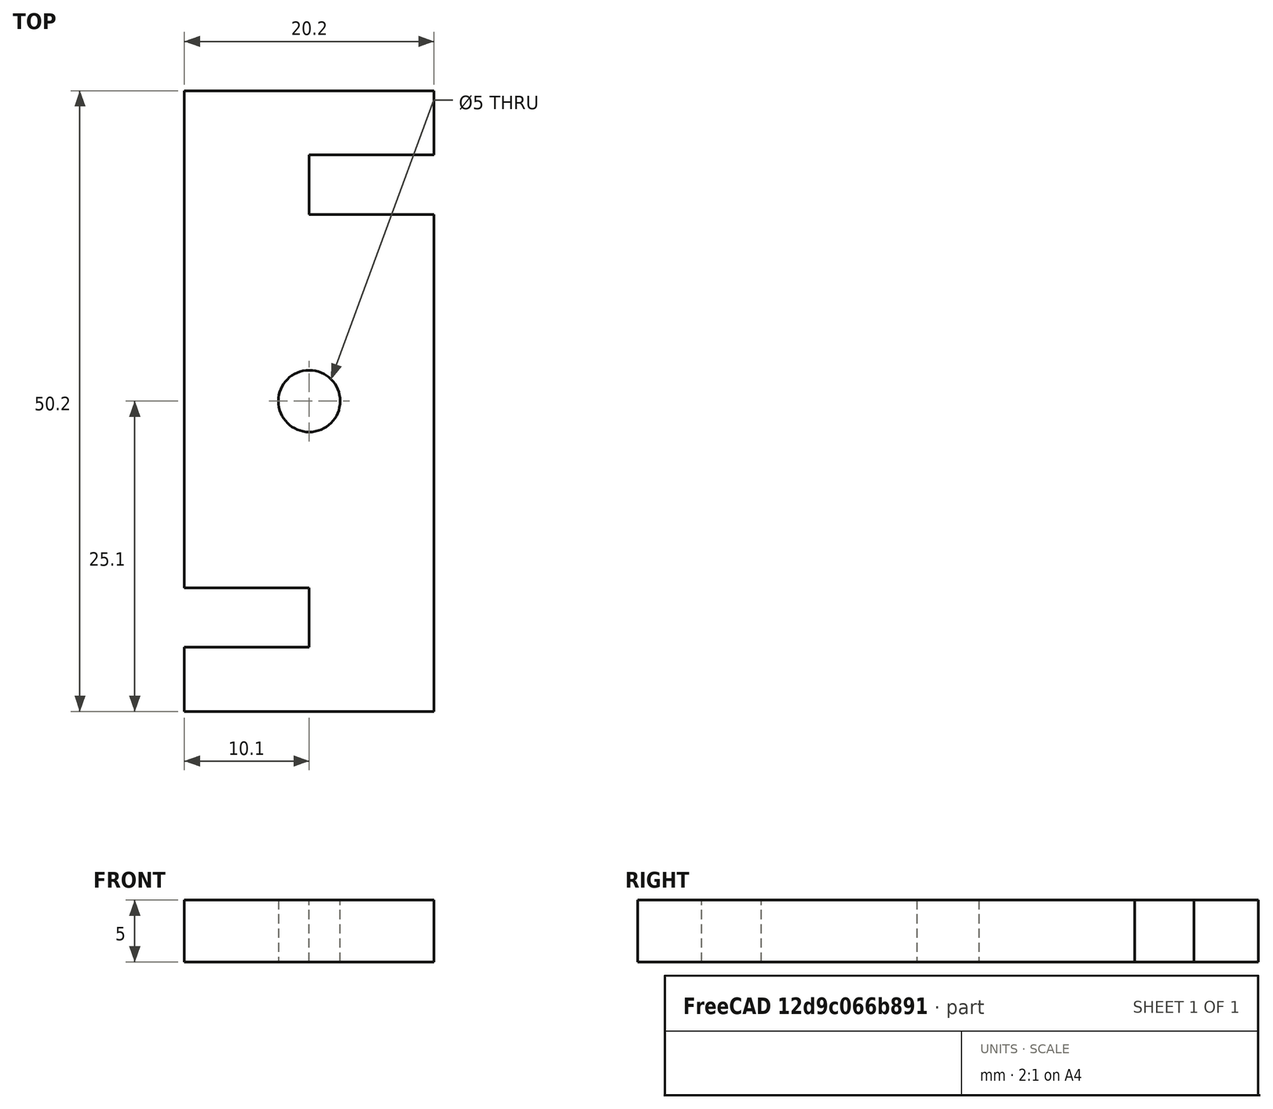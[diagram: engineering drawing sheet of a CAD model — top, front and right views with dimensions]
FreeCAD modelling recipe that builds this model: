
FCSTD DOCUMENT  (FreeCAD 0.16R6707 (Git))
Label: BearingStopAxisMK2
License: All rights reserved
LicenseURL: http://en.wikipedia.org/wiki/All_rights_reserved
objects: Sketcher::SketchObject×1, PartDesign::Pad×1
note: 3 computed .brp shape members not serialized (recipe doc carries the construction recipe); baked Part::Feature solids carry a one-line shape summary decoded from their .brp

FEATURE [Sketcher::SketchObject] Sketch012
  Placement = pos=(0,-5,100) rot=(0,0,1;0rad)
  sketch-geometry (13):
    g0: LineSegment StartX=-10.1 StartY=25.1 StartZ=0 EndX=10.1 EndY=25.1 EndZ=0
    g1: LineSegment StartX=10.1 StartY=25.1 StartZ=0 EndX=10.1 EndY=19.9 EndZ=0
    g2: LineSegment StartX=10.1 StartY=19.9 StartZ=0 EndX=0 EndY=19.9 EndZ=0
    g3: LineSegment StartX=0 StartY=19.9 StartZ=0 EndX=0 EndY=15.1 EndZ=0
    g4: LineSegment StartX=0 StartY=15.1 StartZ=0 EndX=10.1 EndY=15.1 EndZ=0
    g5: LineSegment StartX=10.1 StartY=15.1 StartZ=0 EndX=10.1 EndY=-25.1 EndZ=0
    g6: LineSegment StartX=10.1 StartY=-25.1 StartZ=0 EndX=-10.1 EndY=-25.1 EndZ=0
    g7: LineSegment StartX=-10.1 StartY=-25.1 StartZ=0 EndX=-10.1 EndY=-19.9 EndZ=0
    g8: LineSegment StartX=-10.1 StartY=-19.9 StartZ=0 EndX=0 EndY=-19.9 EndZ=0
    g9: LineSegment StartX=0 StartY=-19.9 StartZ=0 EndX=0 EndY=-15.1 EndZ=0
    g10: LineSegment StartX=0 StartY=-15.1 StartZ=0 EndX=-10.1 EndY=-15.1 EndZ=0
    g11: LineSegment StartX=-10.1 StartY=-15.1 StartZ=0 EndX=-10.1 EndY=25.1 EndZ=0
    g12: Circle CenterX=0 CenterY=0 CenterZ=0 NormalX=0 NormalY=0 NormalZ=1 Radius=2.5
  constraints (36):
    c: Horizontal(g0)
    c: Coincident(g0,g1)
    c: Vertical(g1)
    c: Coincident(g1,g2)
    c: PointOnObject(g2,g-2)
    c: Horizontal(g2)
    c: Coincident(g2,g3)
    c: Vertical(g3)
    c: Coincident(g3,g4)
    c: Horizontal(g4)
    c: Coincident(g4,g5)
    c: Vertical(g5)
    c: Coincident(g5,g6)
    c: Horizontal(g6)
    c: Coincident(g6,g7)
    c: Vertical(g7)
    c: Coincident(g7,g8)
    c: Coincident(g8,g9)
    c: Vertical(g9)
    c: Coincident(g9,g10)
    c: Horizontal(g10)
    c: Coincident(g10,g11)
    c: Coincident(g11,g0)
    c: Vertical(g11)
    c: Horizontal(g8)
    c: Symmetric(g5,g0,g-1)
    c: Symmetric(g6,g5,g-2)
    c: Symmetric(g0,g0,g-2)
    c: Symmetric(g9,g3,g-1)
    c: Symmetric(g8,g2,g-1)
    c: DistanceY(g3) = 15.1
    c: DistanceY(g9,g9) = 4.8
    c: DistanceY(g7,g7) = 5.2
    c: DistanceX(g0,g0) = 20.2
    c: Coincident(g12,g-1)
    c: Radius(g12) = 2.5
FEATURE [PartDesign::Pad] Pad
  Length = 5
  Length2 = 100
  Placement = pos=(0,-5,100) rot=(0,0,1;0rad)
  Sketch = -> Sketch012
  Type = 0
